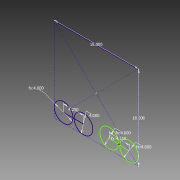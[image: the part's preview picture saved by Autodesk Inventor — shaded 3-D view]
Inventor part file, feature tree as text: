
AUTODESK INVENTOR PART (.ipt)
format: ipt  version: 2015 (Build 190159000, 159)  size: 72,704 bytes
history: native  units: in
note: dims shown in document units (in); Inventor stores cm internally (conversion verified against a paired STEP export)
features: sketch x1
ambient origin geometry x8: Origin, YZ Plane, XZ Plane, XY Plane, X Axis, Y Axis, Z Axis, Center Point
feature tree (1):
  sketch  "Sketch1"  dims[d0=18.0in d1=18.0in d2=4.0in d5=4.0in d6=4.25in d7=4.0in]
